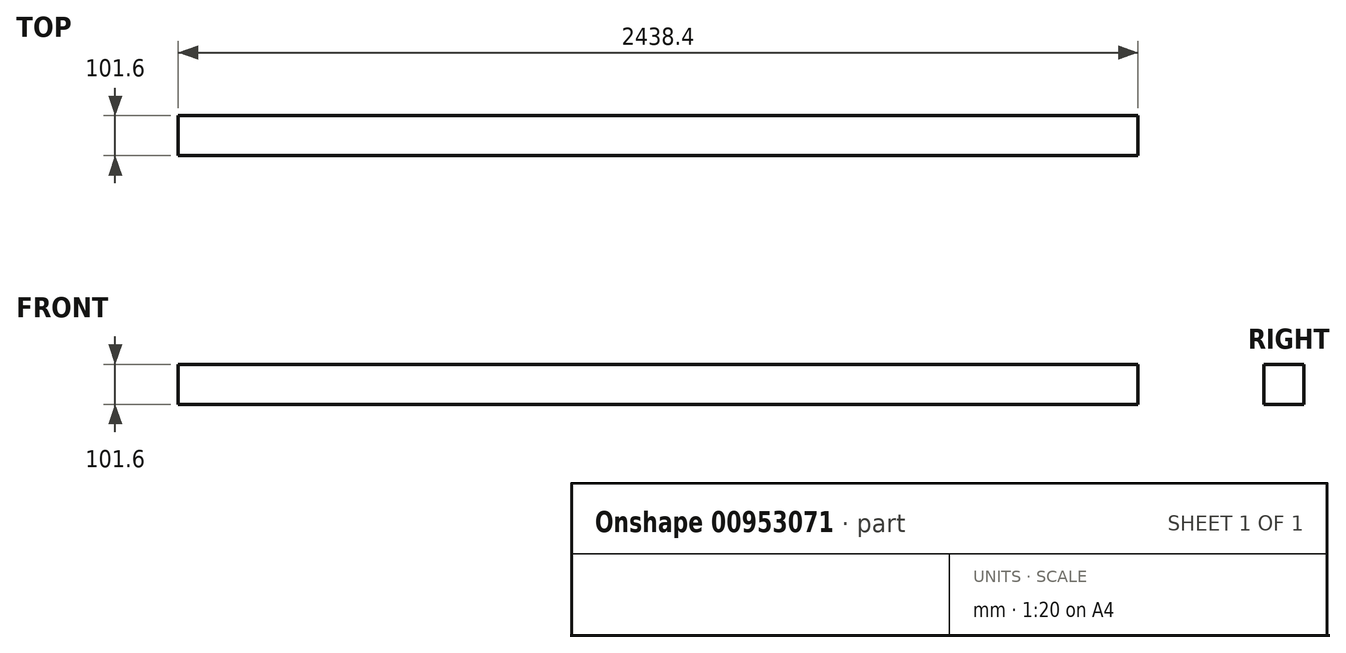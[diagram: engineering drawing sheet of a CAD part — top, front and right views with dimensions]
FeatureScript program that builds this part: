
annotation { "Feature Type Name" : "Feature", "Feature Type Description" : "" }
export const myFeature = defineFeature(function(context is Context, id is Id, definition is map)
    precondition{}
    {
        {
            var Q0;
            Q0=qCreatedBy(makeId("Top.planeOp"),FACE);
            var sketch = newSketch(context, id + "F0", { "sketchPlane" : qUnion([Q0])});
            skLineSegment(sketch, "E0", {"start": v(0, 0) * mm, "end": v(-2438.4, 0) * mm});
            skLineSegment(sketch, "E1", {"start": v(-2438.4, 0) * mm, "end": v(-2438.4, 101.6) * mm});
            skLineSegment(sketch, "E2", {"start": v(-2438.4, 101.6) * mm, "end": v(0, 101.6) * mm});
            skLineSegment(sketch, "E3", {"start": v(0, 101.6) * mm, "end": v(0, 0) * mm});
            skSolve(sketch);
        }
        {
            var Q0;
            Q0 = qSketchRegion(id + "F0", true);
            extrude(context, id + "F1", {"entities" : qUnion([Q0]), "depth" : 101.6 * mm, "offsetDistance" : 25.4 * mm});
        }
    });
